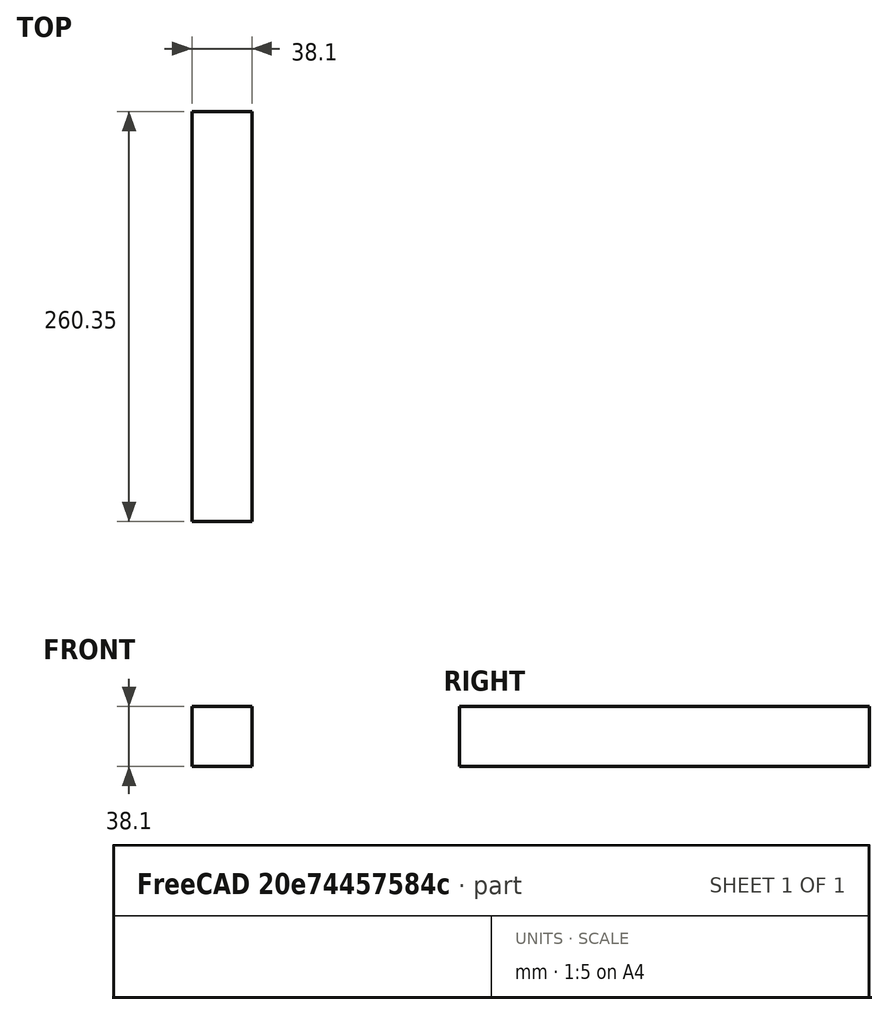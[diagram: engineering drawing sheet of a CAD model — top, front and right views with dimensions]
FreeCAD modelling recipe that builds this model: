
FCSTD DOCUMENT  (FreeCAD 0.19R24291 (Git))
Label: botblock
License: All rights reserved
LicenseURL: http://en.wikipedia.org/wiki/All_rights_reserved
objects: Sketcher::SketchObject×1, PartDesign::Pad×1, PartDesign::Body×1
note: 4 computed .brp shape members not serialized (recipe doc carries the construction recipe); baked Part::Feature solids carry a one-line shape summary decoded from their .brp

FEATURE [Sketcher::SketchObject] Sketch
  FullyConstrained = false
  MapMode = 5
  Placement = pos=(0,0,0) rot=(0.57735,0.57735,0.57735;2.0944rad)
  Support = -> [YZ_Plane]
  sketch-geometry (4):
    g0: LineSegment StartX=-127 StartY=-19.05 StartZ=0 EndX=133.35 EndY=-19.05 EndZ=0
    g1: LineSegment StartX=133.35 StartY=-19.05 StartZ=0 EndX=133.35 EndY=19.05 EndZ=0
    g2: LineSegment StartX=133.35 StartY=19.05 StartZ=0 EndX=-127 EndY=19.05 EndZ=0
    g3: LineSegment StartX=-127 StartY=19.05 StartZ=0 EndX=-127 EndY=-19.05 EndZ=0
  constraints (8):
    c: Coincident(g0,g1)
    c: Coincident(g1,g2)
    c: Coincident(g2,g3)
    c: Coincident(g3,g0)
    c: Horizontal(g0)
    c: Horizontal(g2)
    c: Vertical(g1)
    c: Vertical(g3)
FEATURE [PartDesign::Pad] Pad
  Direction = (1,1,1)
  Length = 38.1
  Length2 = 99.9998
  Placement = pos=(0,0,0) rot=(0.57735,0.57735,0.57735;2.0944rad)
  Profile = -> Sketch
  Refine = true
  Type = 0
FEATURE [PartDesign::Body] Body
  Group = -> [Sketch,Pad]
  Origin = -> Origin
  Tip = -> Pad
